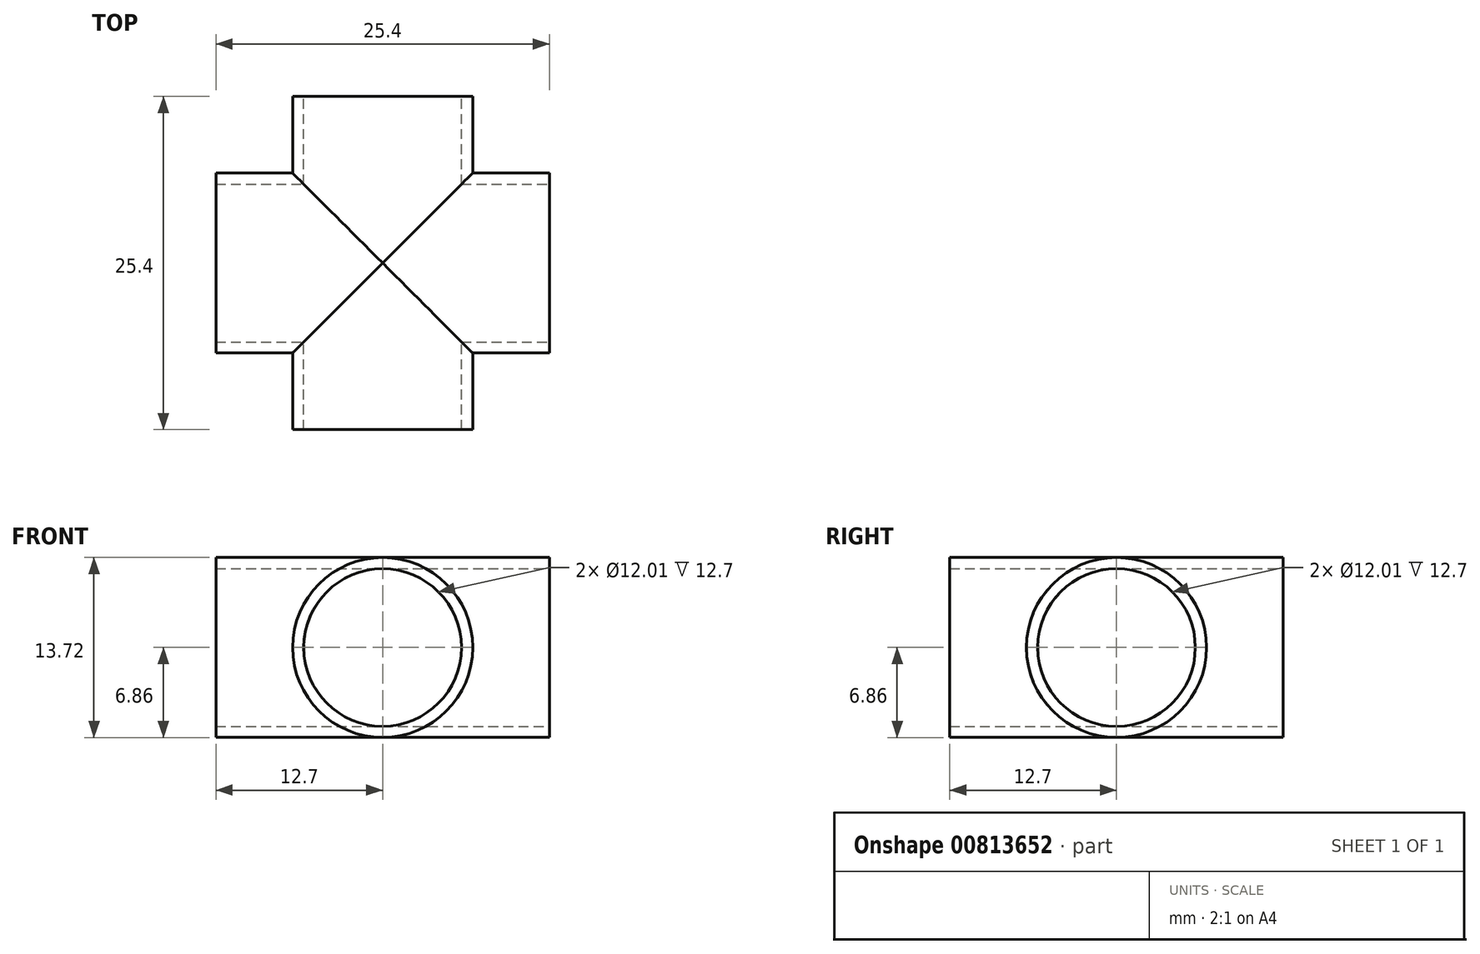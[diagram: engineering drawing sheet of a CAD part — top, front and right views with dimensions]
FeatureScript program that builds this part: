
annotation { "Feature Type Name" : "Feature", "Feature Type Description" : "" }
export const myFeature = defineFeature(function(context is Context, id is Id, definition is map)
    precondition{}
    {
        {
            var Q0;
            Q0=qCreatedBy(makeId("Front.planeOp"),FACE);
            var sketch = newSketch(context, id + "F0", { "sketchPlane" : qUnion([Q0])});
            skCircle(sketch, "E0", {"center": v(0, 0) * mm, "radius": 6.86 * mm});
            skCircle(sketch, "E1", {"center": v(0, 0) * mm, "radius": 5.16 * mm});
            skSolve(sketch);
        }
        {
            var Q0;
            Q0=makeQuery(id+"F0.imprint","IMPRINT",FACE,{"disambiguationData":[TD([[makeQuery(id+"F0.imprint","IMPRINT",EDGE,{"derivedFrom":sQuery(id+"F0.wireOp",EDGE,"E1")}),1.0]])]});
            var Q1;
            Q1=makeQuery(id+"F0.imprint","IMPRINT",FACE,{"disambiguationData":[TD([[makeQuery(id+"F0.imprint","IMPRINT",EDGE,{"derivedFrom":sQuery(id+"F0.wireOp",EDGE,"E0")}),1.0]])]});
            extrude(context, id + "F1", {"entities" : qUnion([Q0, Q1]), "endBound" : BoundingType.SYMMETRIC, "depth" : 25.4 * mm, "offsetDistance" : 25.4 * mm});
        }
        {
            var Q0;
            Q0=qCreatedBy(makeId("Right.planeOp"),FACE);
            var sketch = newSketch(context, id + "F2", { "sketchPlane" : qUnion([Q0])});
            skCircle(sketch, "E2", {"center": v(0, 0) * mm, "radius": 6.86 * mm});
            skCircle(sketch, "E3", {"center": v(0, 0) * mm, "radius": 5.16 * mm});
            skSolve(sketch);
        }
        {
            var Q0;
            Q0=makeQuery(id+"F2.imprint","IMPRINT",FACE,{"disambiguationData":[TD([[makeQuery(id+"F2.imprint","IMPRINT",EDGE,{"derivedFrom":sQuery(id+"F2.wireOp",EDGE,"E3")}),1.0]])]});
            var Q1;
            Q1=makeQuery(id+"F2.imprint","IMPRINT",FACE,{"disambiguationData":[TD([[makeQuery(id+"F2.imprint","IMPRINT",EDGE,{"derivedFrom":sQuery(id+"F2.wireOp",EDGE,"E2")}),1.0]])]});
            extrude(context, id + "F3", {"entities" : qUnion([Q0, Q1]), "operationType" : NewBodyOperationType.ADD, "endBound" : BoundingType.SYMMETRIC, "depth" : 25.4 * mm, "offsetDistance" : 25.4 * mm});
        }
        {
            var Q0;
            Q0=qCreatedBy(makeId("Right.planeOp"),FACE);
            var sketch = newSketch(context, id + "F4", { "sketchPlane" : qUnion([Q0])});
            skCircle(sketch, "E4", {"center": v(0, 0) * mm, "radius": 6 * mm});
            skSolve(sketch);
        }
        {
            var Q0;
            Q0 = qSketchRegion(id + "F4", true);
            extrude(context, id + "F5", {"entities" : qUnion([Q0]), "operationType" : NewBodyOperationType.REMOVE, "endBound" : BoundingType.SYMMETRIC, "oppositeDirection" : true, "depth" : 25.4 * mm, "offsetDistance" : 25.4 * mm});
        }
        {
            var Q0;
            Q0=qCreatedBy(makeId("Front.planeOp"),FACE);
            var sketch = newSketch(context, id + "F6", { "sketchPlane" : qUnion([Q0])});
            skCircle(sketch, "E5", {"center": v(0, 0) * mm, "radius": 6 * mm});
            skSolve(sketch);
        }
        {
            var Q0;
            Q0 = qSketchRegion(id + "F6", true);
            extrude(context, id + "F7", {"entities" : qUnion([Q0]), "operationType" : NewBodyOperationType.REMOVE, "endBound" : BoundingType.SYMMETRIC, "depth" : 25.4 * mm, "offsetDistance" : 25.4 * mm});
        }
    });
